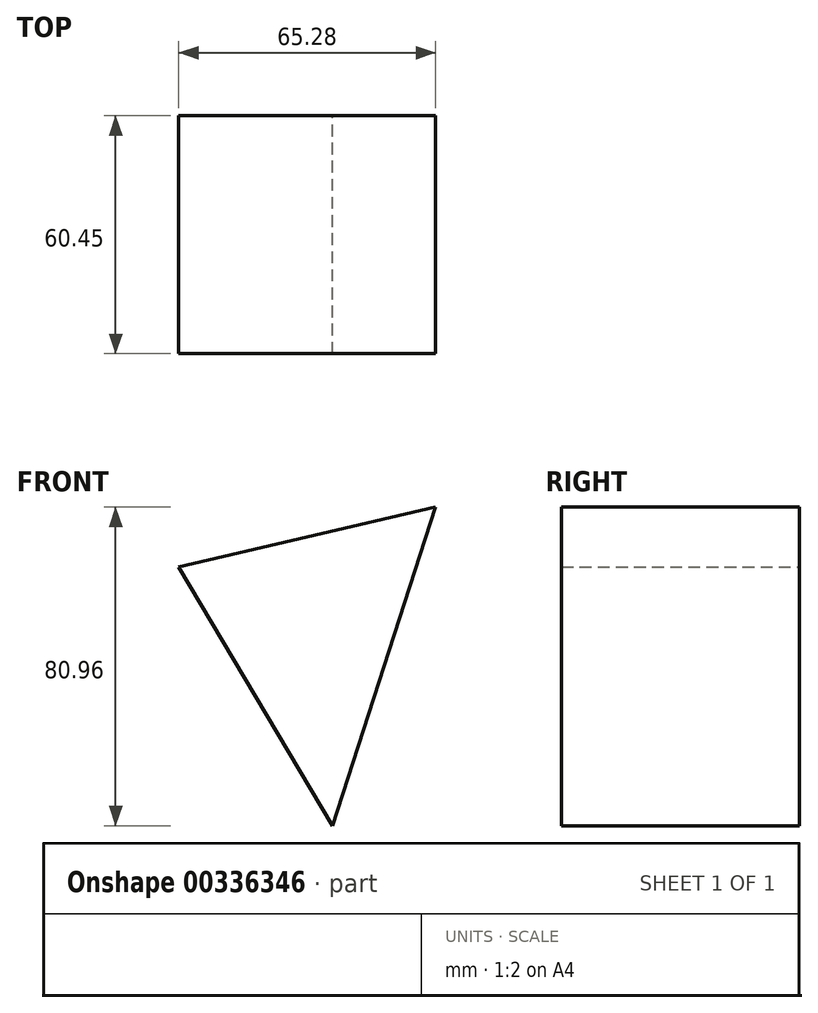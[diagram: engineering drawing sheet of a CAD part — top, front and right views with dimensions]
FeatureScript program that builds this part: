
annotation { "Feature Type Name" : "Feature", "Feature Type Description" : "" }
export const myFeature = defineFeature(function(context is Context, id is Id, definition is map)
    precondition{}
    {
        {
            var Q0;
            Q0=qCreatedBy(makeId("Front.planeOp"),FACE);
            var sketch = newSketch(context, id + "F0", { "sketchPlane" : qUnion([Q0])});
            skLineSegment(sketch, "E0", {"start": v(-108.26, 30.72) * mm, "end": v(-134.44, -50.24) * mm});
            skLineSegment(sketch, "E1", {"start": v(-134.44, -50.24) * mm, "end": v(-173.54, 15.56) * mm});
            skLineSegment(sketch, "E2", {"start": v(-173.54, 15.56) * mm, "end": v(-108.26, 30.72) * mm});
            skSolve(sketch);
        }
        {
            var Q0;
            Q0=makeQuery(id+"F0.imprint","IMPRINT",FACE,{"disambiguationData":[TD([[makeQuery(id+"F0.imprint","IMPRINT",EDGE,{"derivedFrom":sQuery(id+"F0.wireOp",EDGE,"E0")}),-1.0]])]});
            extrude(context, id + "F1", {"entities" : qUnion([Q0]), "depth" : 60.45 * mm});
        }
    });
